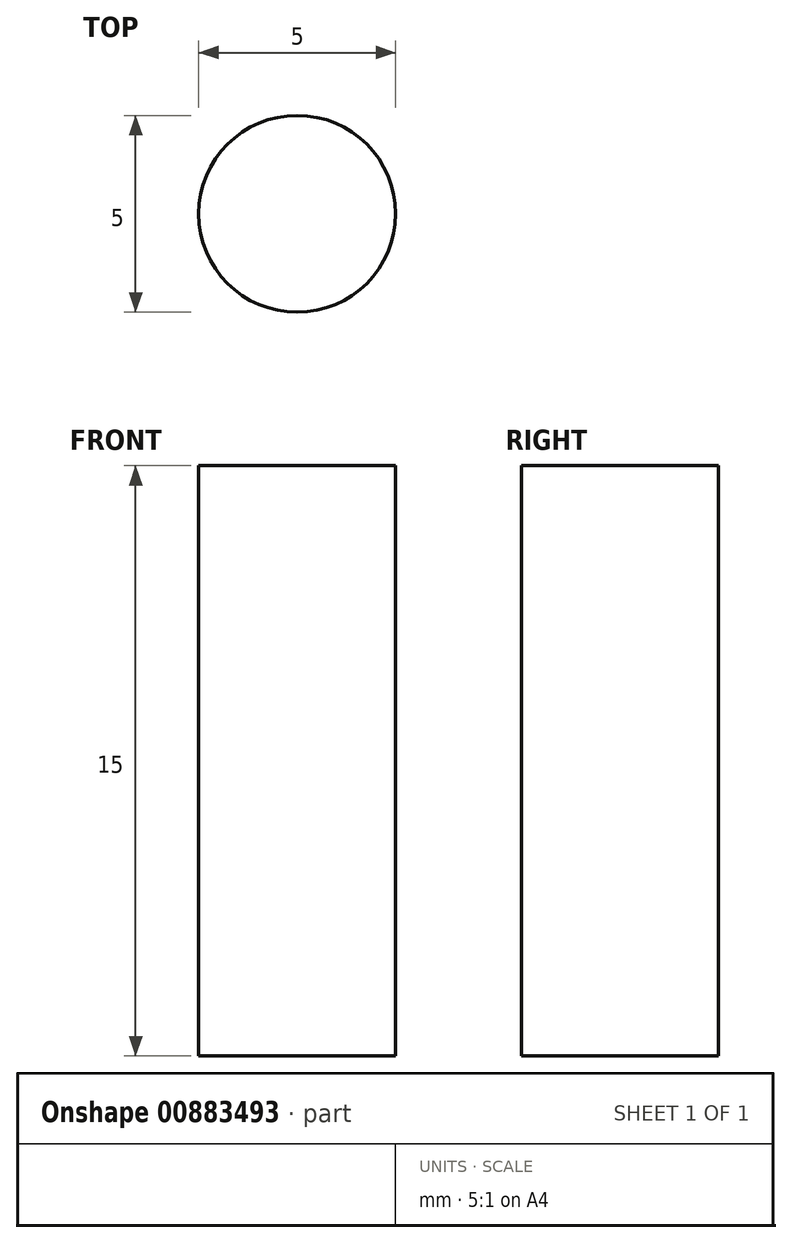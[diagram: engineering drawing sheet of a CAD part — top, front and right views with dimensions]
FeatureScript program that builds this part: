
annotation { "Feature Type Name" : "Feature", "Feature Type Description" : "" }
export const myFeature = defineFeature(function(context is Context, id is Id, definition is map)
    precondition{}
    {
        {
            var Q0;
            Q0=qCreatedBy(makeId("Top.planeOp"),FACE);
            var sketch = newSketch(context, id + "F0", { "sketchPlane" : qUnion([Q0])});
            skCircle(sketch, "E0", {"center": v(0, 0) * mm, "radius": 2.5 * mm});
            skLineSegment(sketch, "E1", {"start": v(-2.5, 0) * mm, "end": v(2.5, 0) * mm, "construction": true});
            skSolve(sketch);
        }
        {
            var Q0;
            Q0=qCreatedBy(makeId("Front.planeOp"),FACE);
            var sketch = newSketch(context, id + "F1", { "sketchPlane" : qUnion([Q0])});
            skLineSegment(sketch, "E2.bottom", {"start": v(-2.5, 15) * mm, "end": v(2.5, 15) * mm});
            skLineSegment(sketch, "E2.top", {"start": v(-2.5, 0) * mm, "end": v(2.5, 0) * mm});
            skLineSegment(sketch, "E2.left", {"start": v(-2.5, 15) * mm, "end": v(-2.5, 0) * mm});
            skLineSegment(sketch, "E2.right", {"start": v(2.5, 15) * mm, "end": v(2.5, 0) * mm});
            skSolve(sketch);
        }
        {
            var Q0;
            Q0=makeQuery(id+"F0.imprint","IMPRINT",FACE,{"disambiguationData":[TD([[makeQuery(id+"F0.imprint","IMPRINT",EDGE,{"derivedFrom":sQuery(id+"F0.wireOp",EDGE,"E0")}),1.0]])]});
            var Q1;
            Q1=sQuery(id+"F1.wireOp",VERTEX,"E2.bottom.start");
            extrude(context, id + "F2", {"entities" : qUnion([Q0]), "endBound" : BoundingType.UP_TO_VERTEX, "depth" : 25 * mm, "endBoundEntityVertex" : qUnion([Q1]), "offsetDistance" : 25 * mm});
        }
        {
            var Q0;
            Q0=qCreatedBy(makeId("Top.planeOp"),FACE);
            var Q1;
            Q1=sQuery(id+"F1.wireOp",VERTEX,"E2.bottom.start");
            cPlane(context, id + "F3", {"entities" : qUnion([Q0, Q1]), "cplaneType" : CPlaneType.PLANE_POINT, "offset" : 0 * mm, "width" : 150 * mm, "height" : 150 * mm});
        }
        {
            var Q0;
            Q0=qCreatedBy(id+"F3.planeOp",FACE);
            var sketch = newSketch(context, id + "F4", { "sketchPlane" : qUnion([Q0])});
            skCircle(sketch, "E3", {"center": v(0, 0) * mm, "radius": 2.5 * mm});
            skSolve(sketch);
        }
    });
